# Revit family: Grundplatten Typ 0
name_source: partatom
category: HLS-Bauteile
revit_build: Autodesk Revit 2017 (Build: 20190507_1515(x64)
units: mm (PartAtom-declared; Revit-internal decimal feet)

## family parameters
Arbeitsebenenbasiert = Ja
Beim Laden mit Abzugskörper schneiden = Nein
Bemaßung runder Anschluss = Durchmesser verwenden
Gemeinsam genutzt = Ja
Immer vertikal = Nein
OmniClass-Nummer = 23.75.00.00
OmniClass-Titel = Climate Control (HVAC)
Raumberechnungspunkt = Nein
Teiletyp = Normal

## types (2) — shared parameters
Abmessung = 80 x 30 x 3 mm
Abstand zur Außenkante = 13 mm  [stored 0.0426509 ft]
Anzahl Befestigungsloch = 2
Breite = 30 mm  [stored 0.0984252 ft]
Fabrikat = MEFA
Firma = MEFA Befestigungs- und Montagesysteme GmbH
Höhe Gewindeanschluss HGW = 15 mm  [stored 0.0492126 ft]
Kurztext1 = Grundplatte Typ 0
Lochabstand längs = 55 mm
Lochdurchmesser = 10,5 mm
Länge = 80 mm  [stored 0.262467 ft]
Material = Stahl
Materialname = S235
Mengeneinheit = St
Oberflaeche = galvanisch verzinkt
Stärke = 3 mm  [stored 0.00984252 ft]
max. zul. Last hängend = 1.05 kN
vpe = 50 St
zero-valued in all types: Sicherheitsfaktor, Vorgabe-Ansicht

## per-type parameters (varying)
| type | Anschluss | Anschlüsse | Artikelnummer | EAN | Gewicht | Gewicht pro Bauteil | Kurztext2 |
| Grundplatte Typ 0 80x30x3,0 M 8 | M8 | 6kt-Mutter parametrik : Hutmutter gedreht M8 (4130008) | 05900008 | 4250928414922 | 0.06 kg | 0.06 kg | Anschluss M8 Platte 80x30x3 mm |
| Grundplatte Typ 0 80x30x3,0 M10 | M10 | 6kt-Mutter parametrik : Hutmutter gedreht M10 (4130010) | 05900010 | 4250928414939 | 0.07 kg | 0.07 kg | Anschluss M10 Platte 80x30x3 mm |

note: [stored X ft] marks values corroborated as IEEE doubles in the binary element streams (Revit-internal decimal feet)

## geometry (parser evidence)
native form markers: Sweep x3
no freeform markers — native parametric forms only
